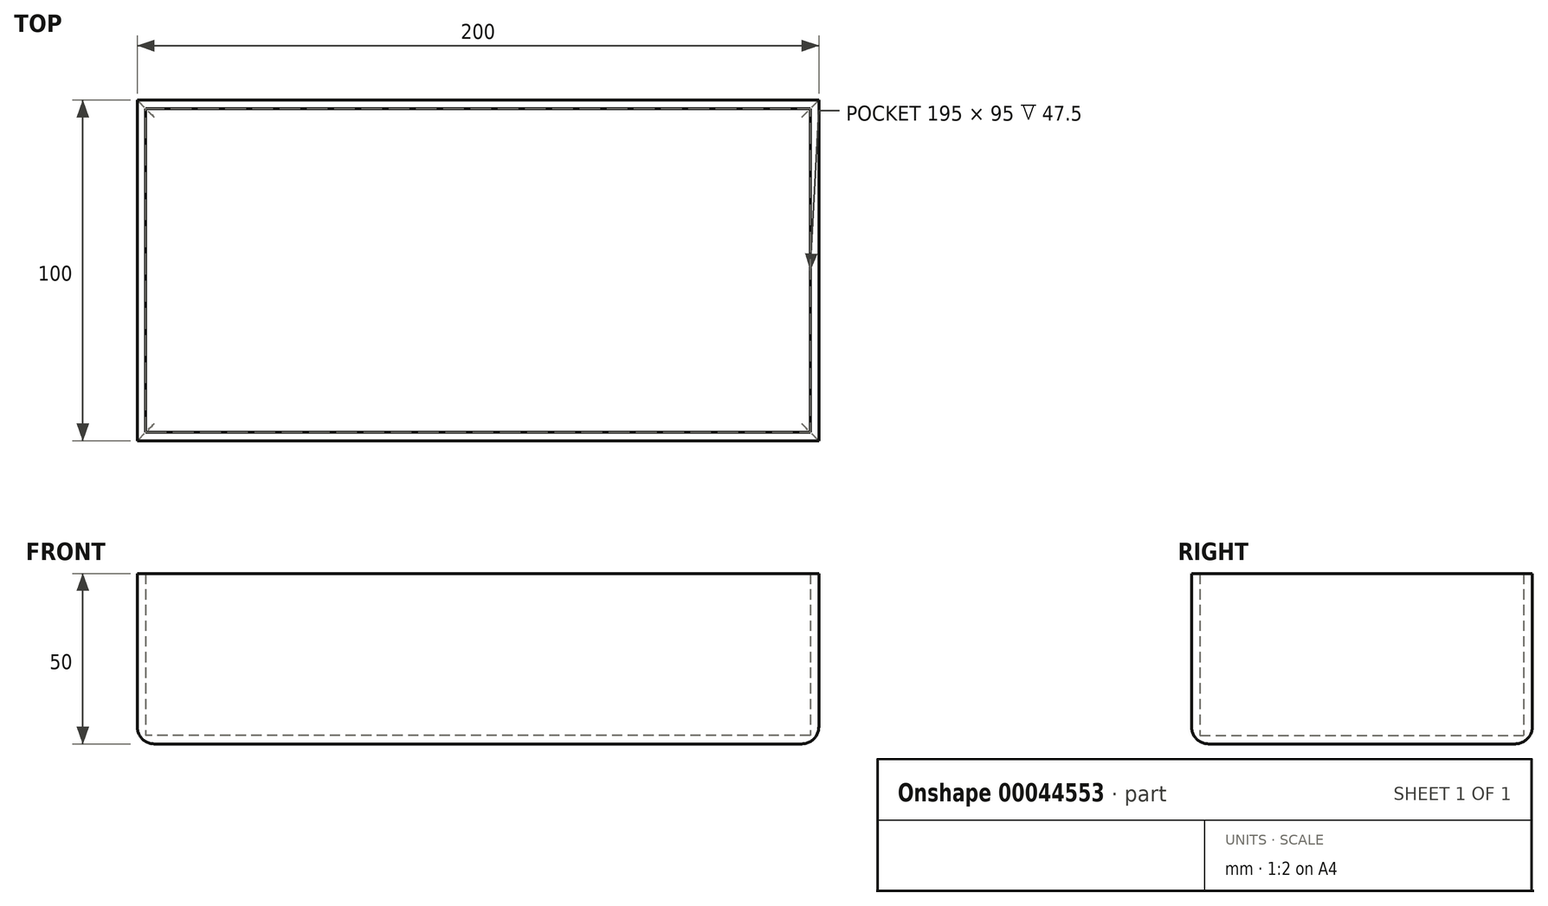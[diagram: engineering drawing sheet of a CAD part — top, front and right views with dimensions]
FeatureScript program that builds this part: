
annotation { "Feature Type Name" : "Feature", "Feature Type Description" : "" }
export const myFeature = defineFeature(function(context is Context, id is Id, definition is map)
    precondition{}
    {
        {
            var Q0;
            Q0=qCreatedBy(makeId("Top.planeOp"),FACE);
            var sketch = newSketch(context, id + "F0", { "sketchPlane" : qUnion([Q0])});
            skLineSegment(sketch, "E0.rect.bottom", {"start": v(100, -50) * mm, "end": v(-100, -50) * mm});
            skLineSegment(sketch, "E0.rect.top", {"start": v(100, 50) * mm, "end": v(-100, 50) * mm});
            skLineSegment(sketch, "E0.rect.left", {"start": v(100, -50) * mm, "end": v(100, 50) * mm});
            skLineSegment(sketch, "E0.rect.right", {"start": v(-100, -50) * mm, "end": v(-100, 50) * mm});
            skPoint(sketch, "E0.rect.middle", {"position": v(0, 0) * mm});
            skSolve(sketch);
        }
        {
            var Q0;
            Q0=makeQuery(id+"F0.imprint","IMPRINT",FACE,{"disambiguationData":[TD([[makeQuery(id+"F0.imprint","IMPRINT",EDGE,{"derivedFrom":sQuery(id+"F0.wireOp",EDGE,"E0.rect.bottom")}),-1.0]])]});
            extrude(context, id + "F1", {"entities" : qUnion([Q0]), "depth" : 50 * mm});
        }
        {
            var Q0;
            Q0=makeQuery(id+"F1.opExtrude","CAP_FACE",FACE,{"disambiguationData":[OSD([sQuery(id+"F0.wireOp",EDGE,"E0.rect.bottom"),sQuery(id+"F0.wireOp",EDGE,"E0.rect.top"),sQuery(id+"F0.wireOp",EDGE,"E0.rect.left"),sQuery(id+"F0.wireOp",EDGE,"E0.rect.right")])],"isStart":false});
            shell(context, id + "F2", {"entities" : qUnion([Q0]), "thickness" : 2.5 * mm});
        }
        {
            var Q0;
            Q0=makeQuery(id+"F1.opExtrude","CAP_FACE",FACE,{"disambiguationData":[OSD([sQuery(id+"F0.wireOp",EDGE,"E0.rect.bottom"),sQuery(id+"F0.wireOp",EDGE,"E0.rect.top"),sQuery(id+"F0.wireOp",EDGE,"E0.rect.left"),sQuery(id+"F0.wireOp",EDGE,"E0.rect.right")])],"isStart":true});
            fillet(context, id + "F3", {"entities" : qUnion([Q0]), "radius" : 5 * mm, "tangentPropagation" : true, "allowEdgeOverflow" : false});
        }
    });
